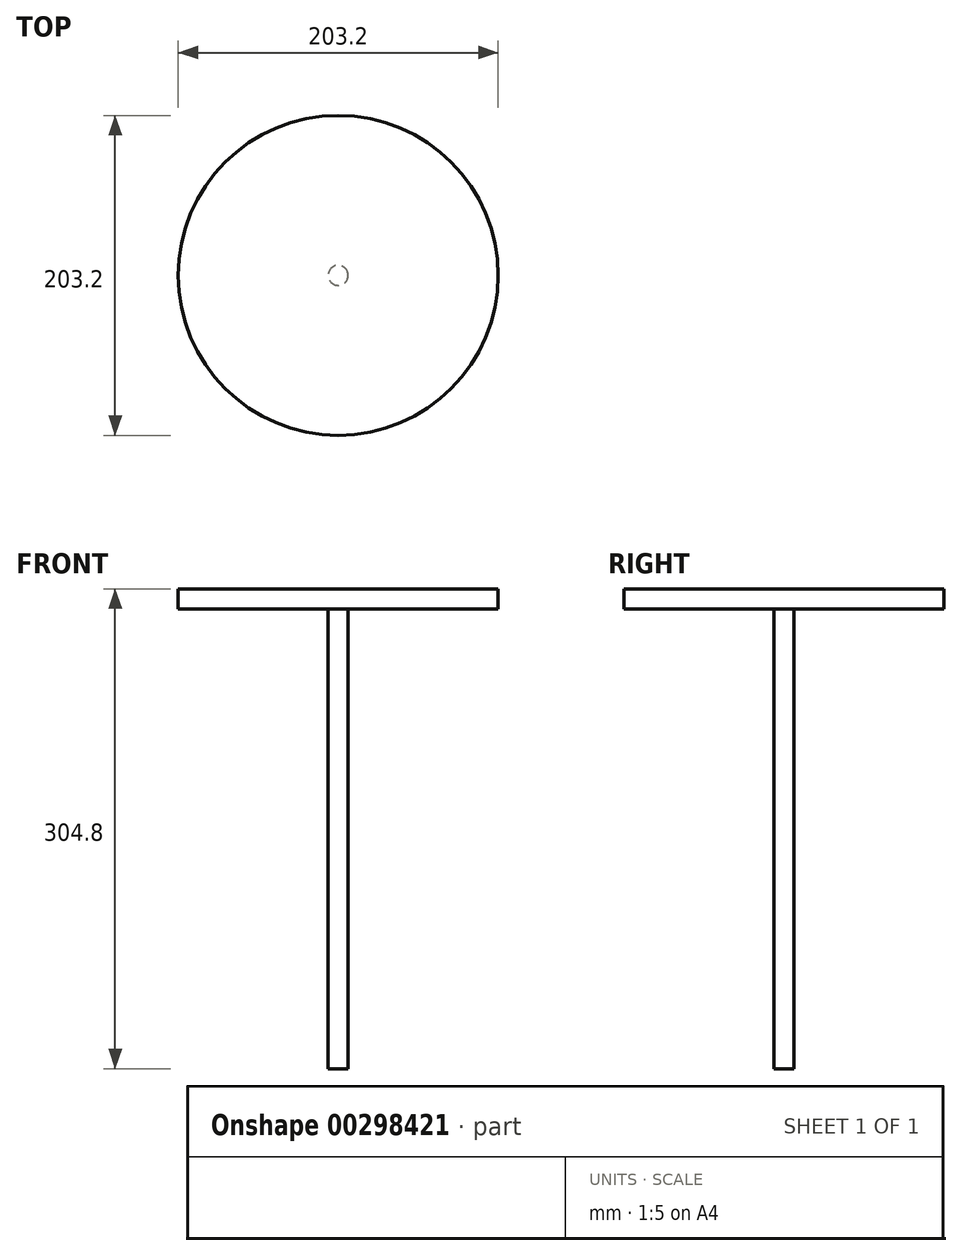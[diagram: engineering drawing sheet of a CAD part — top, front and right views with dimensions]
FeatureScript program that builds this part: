
annotation { "Feature Type Name" : "Feature", "Feature Type Description" : "" }
export const myFeature = defineFeature(function(context is Context, id is Id, definition is map)
    precondition{}
    {
        {
            var Q0;
            Q0=qCreatedBy(makeId("Front.planeOp"),FACE);
            var sketch = newSketch(context, id + "F0", { "sketchPlane" : qUnion([Q0])});
            skLineSegment(sketch, "E0", {"start": v(0, 0) * mm, "end": v(0, 304.8) * mm});
            skLineSegment(sketch, "E1", {"start": v(0, 304.8) * mm, "end": v(101.6, 304.8) * mm});
            skLineSegment(sketch, "E2", {"start": v(101.6, 304.8) * mm, "end": v(101.6, 292.1) * mm});
            skLineSegment(sketch, "E3", {"start": v(101.6, 292.1) * mm, "end": v(6.35, 292.1) * mm});
            skLineSegment(sketch, "E4", {"start": v(6.35, 292.1) * mm, "end": v(6.35, 0) * mm});
            skLineSegment(sketch, "E5", {"start": v(6.35, 0) * mm, "end": v(0, 0) * mm});
            skSolve(sketch);
        }
        {
            var Q0;
            Q0 = qSketchRegion(id + "F0", true);
            var Q1;
            Q1=sQuery(id+"F0.wireOp",EDGE,"E0");
            revolve(context, id + "F1", {"entities" : qUnion([Q0]), "axis" : qUnion([Q1]), "revolveType" : RevolveType.FULL});
        }
    });
